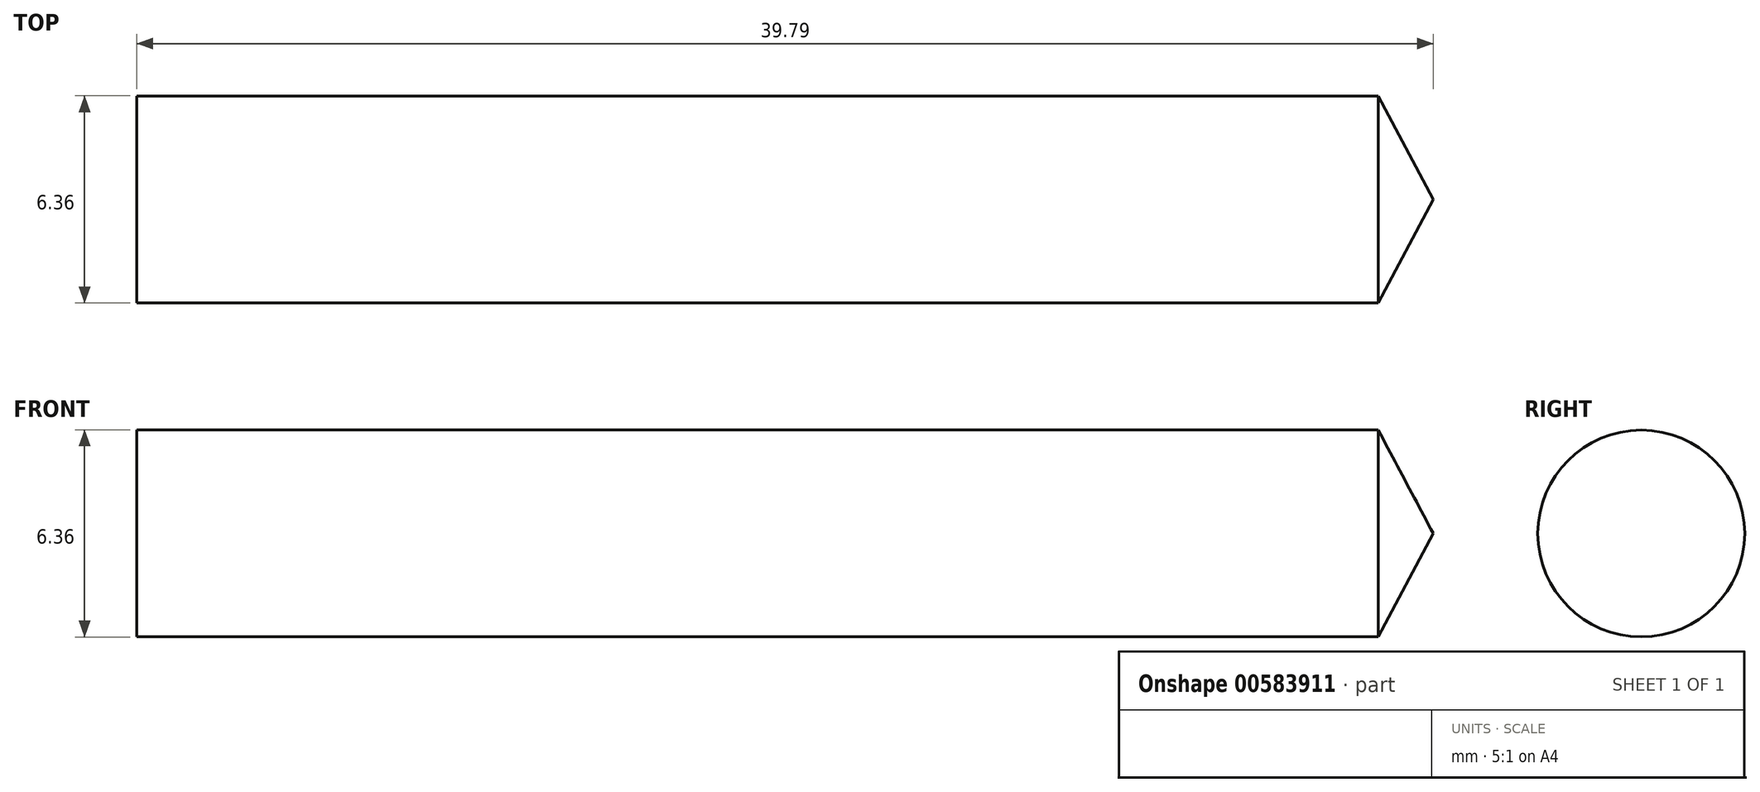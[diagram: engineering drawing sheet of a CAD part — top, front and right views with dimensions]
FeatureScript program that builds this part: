
annotation { "Feature Type Name" : "Feature", "Feature Type Description" : "" }
export const myFeature = defineFeature(function(context is Context, id is Id, definition is map)
    precondition{}
    {
        {
            var Q0;
            Q0=qCreatedBy(makeId("Front.planeOp"),FACE);
            var sketch = newSketch(context, id + "F0", { "sketchPlane" : qUnion([Q0])});
            skLineSegment(sketch, "E0.bottom", {"start": v(0, 3.17) * mm, "end": v(38.1, 3.17) * mm});
            skLineSegment(sketch, "E0.top", {"start": v(0, -3.18) * mm, "end": v(38.1, -3.17) * mm});
            skLineSegment(sketch, "E0.left", {"start": v(0, 3.18) * mm, "end": v(0, -3.18) * mm});
            skLineSegment(sketch, "E0.right", {"start": v(38.1, 3.17) * mm, "end": v(38.1, -3.17) * mm});
            skPoint(sketch, "E1", {"position": v(0, 0) * mm});
            skLineSegment(sketch, "E2", {"start": v(39.79, 0) * mm, "end": v(38.1, -3.17) * mm});
            skLineSegment(sketch, "E3", {"start": v(39.79, 0) * mm, "end": v(38.1, 3.18) * mm});
            skCircle(sketch, "E4", {"center": v(38.1, 0) * mm, "radius": 3.18 * mm, "construction": true});
            skLineSegment(sketch, "E5", {"start": v(36.4, -2.69) * mm, "end": v(39.8, 2.69) * mm, "construction": true});
            skLineSegment(sketch, "E6", {"start": v(35.88, 1.4) * mm, "end": v(38.1, 0) * mm, "construction": true});
            skLineSegment(sketch, "E7", {"start": v(38.1, 0) * mm, "end": v(40.32, -1.4) * mm, "construction": true});
            skLineSegment(sketch, "E8", {"start": v(39.79, 0) * mm, "end": v(0, 0) * mm, "construction": true});
            skSolve(sketch);
        }
        {
            var Q0;
            Q0=qCreatedBy(makeId("Front.planeOp"),FACE);
            var sketch = newSketch(context, id + "F1", { "sketchPlane" : qUnion([Q0])});
            skLineSegment(sketch, "E9.bottom", {"start": v(0, 3.18) * mm, "end": v(38.1, 3.18) * mm});
            skLineSegment(sketch, "E9.top", {"start": v(0, 0) * mm, "end": v(38.1, 0) * mm});
            skLineSegment(sketch, "E9.left", {"start": v(0, 3.18) * mm, "end": v(0, 0) * mm});
            skLineSegment(sketch, "E9.right", {"start": v(38.1, 3.18) * mm, "end": v(38.1, 0) * mm, "construction": true});
            skLineSegment(sketch, "E10", {"start": v(38.1, 0) * mm, "end": v(39.79, 0) * mm});
            skLineSegment(sketch, "E11", {"start": v(39.79, 0) * mm, "end": v(38.1, 3.18) * mm});
            skSolve(sketch);
        }
        {
            var Q0;
            Q0 = qSketchRegion(id + "F1", true);
            var Q1;
            Q1=sQuery(id+"F1.wireOp",EDGE,"E9.top");
            revolve(context, id + "F2", {"entities" : qUnion([Q0]), "axis" : qUnion([Q1]), "revolveType" : RevolveType.FULL});
        }
        {
            var Q0;
            Q0=sQuery(id+"F0.wireOp",EDGE,"E7");
            cPlane(context, id + "F3", {"entities" : qUnion([Q0]), "cplaneType" : CPlaneType.LINE_ANGLE, "offset" : 25.4 * mm, "angle" : 115 * degree, "width" : 152.4 * mm, "height" : 152.4 * mm});
        }
        {
            var Q0;
            Q0=qCreatedBy(id+"F3.planeOp",FACE);
            var sketch = newSketch(context, id + "F4", { "sketchPlane" : qUnion([Q0])});
            skCircle(sketch, "E12", {"center": v(33.37, 0) * mm, "radius": 3.18 * mm});
            skSolve(sketch);
        }
        {
            var Q0;
            Q0=qCreatedBy(makeId("Front.planeOp"),FACE);
            var sketch = newSketch(context, id + "F5", { "sketchPlane" : qUnion([Q0])});
            skEllipse(sketch, "E13", {"center": v(38.1, 0) * mm, "majorRadius": 3.18 * mm, "minorRadius": 1.34 * mm, "majorAxis": v(-0.85, 0.53)});
            skLineSegment(sketch, "E14", {"start": v(35.41, 1.7) * mm, "end": v(38.1, 0) * mm, "construction": true});
            skLineSegment(sketch, "E15", {"start": v(37.39, -1.14) * mm, "end": v(38.1, 0) * mm, "construction": true});
            skLineSegment(sketch, "E16", {"start": v(38.81, 1.14) * mm, "end": v(38.1, 0) * mm, "construction": true});
            skLineSegment(sketch, "E17", {"start": v(40.79, -1.7) * mm, "end": v(38.1, 0) * mm, "construction": true});
            skEllipse(sketch, "E18", {"center": v(35.32, 0) * mm, "majorRadius": 3.18 * mm, "minorRadius": 1.34 * mm, "majorAxis": v(0.85, -0.53)});
            skLineSegment(sketch, "E19", {"start": v(32.63, 1.7) * mm, "end": v(35.32, 0) * mm, "construction": true});
            skLineSegment(sketch, "E20", {"start": v(38, -1.7) * mm, "end": v(35.32, 0) * mm, "construction": true});
            skLineSegment(sketch, "E21", {"start": v(34.6, -1.14) * mm, "end": v(35.32, 0) * mm, "construction": true});
            skLineSegment(sketch, "E22", {"start": v(36.03, 1.14) * mm, "end": v(35.32, 0) * mm, "construction": true});
            skSolve(sketch);
        }
        {
            var Q0;
            Q0=sQuery(id+"F5.wireOp",EDGE,"E19");
            cPlane(context, id + "F6", {"entities" : qUnion([Q0]), "cplaneType" : CPlaneType.LINE_ANGLE, "offset" : 25.4 * mm, "angle" : 115 * degree, "width" : 152.4 * mm, "height" : 152.4 * mm});
        }
    });
